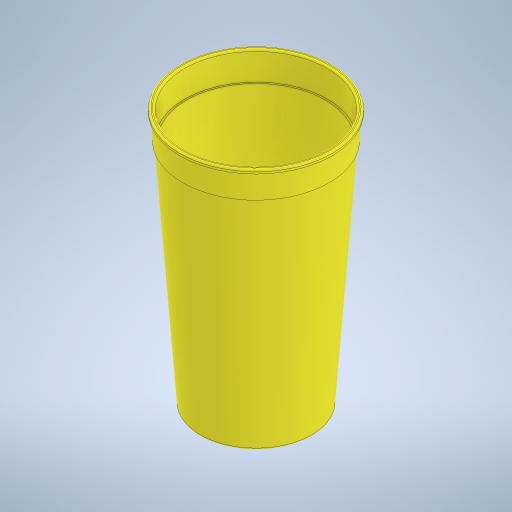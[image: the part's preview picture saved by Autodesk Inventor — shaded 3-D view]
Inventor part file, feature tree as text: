
AUTODESK INVENTOR PART (.ipt)
format: ipt  version: 2024 (Build 280153000, 153)  size: 300,032 bytes
history: native  units: in
note: dims shown in document units (in); Inventor stores cm internally (conversion verified against a paired STEP export)
features: sketch x4, plane x2, fillet x2, extrude x2, loft x1, delete_face x1, thicken_offset x1, projected_geometry x1
ambient origin geometry x8: Origin, YZ Plane, XZ Plane, XY Plane, X Axis, Y Axis, Z Axis, Center Point
bodies: Solid1 (feature_tree)
feature tree (14):
  sketch  "Sketch1"  dims[d0=2.94in d1=0.0in d2=6.035in d3=3.8in]
  plane  "Work Plane2"
  loft  "Loft1"
  delete_face  "Delete Face1"
  thicken_offset  "Thicken1"
  fillet  "Fillet1"  Radius=3.8in
  extrude  "Extrusion1"  TaperAngle=0.0deg  [1 undecoded]
  extrude  "Extrusion2"  Depth=0.05in
  fillet  "Fillet2"  Radius=4.02in
  plane  "Work Plane1"
  sketch  "Sketch2"  dims[d4=0.0in d5=90.0deg d6=0.0in d7=90.0deg]
  sketch  "Sketch3"  dims[d8=0.065in d9=0.05in d10=4.02in]
  sketch  "Sketch4"  dims[d11=0.077in d12=0.652in d13=0.0in d14=4.02in d15=0.102in d16=0.0in d17=0.05in]
  projected_geometry  "Projected Loop1"
note: 1 required parameter value undecoded (feature->parameter linkage not recoverable at this tier; creation-order binding heuristic only, values carry confidence <= 0.55)
